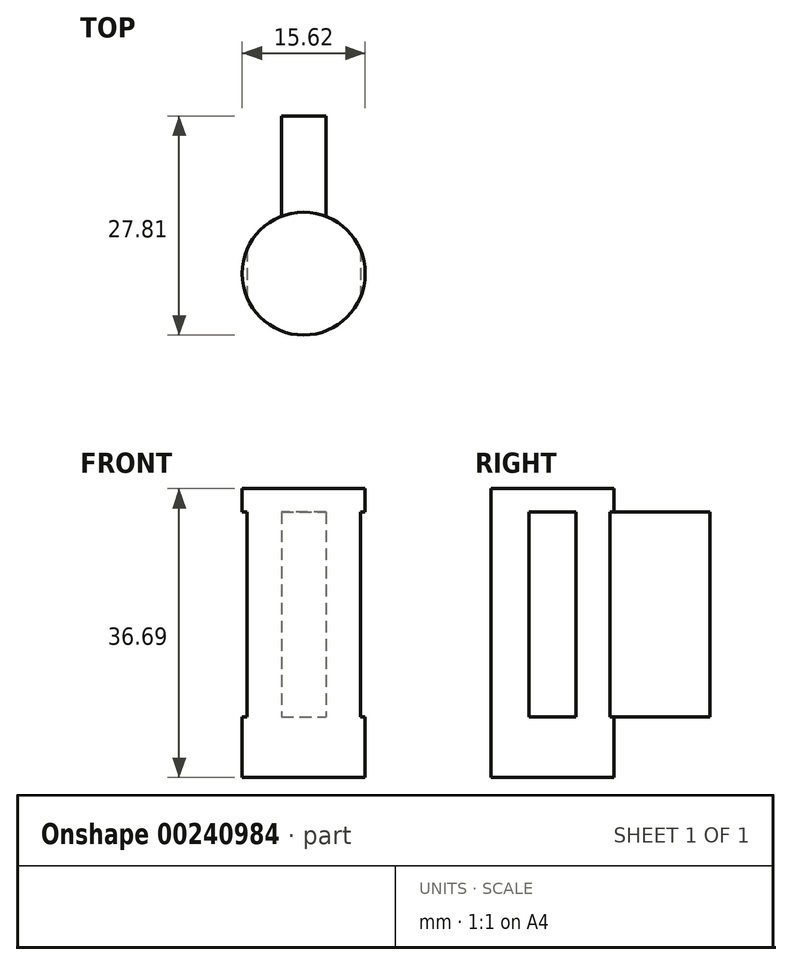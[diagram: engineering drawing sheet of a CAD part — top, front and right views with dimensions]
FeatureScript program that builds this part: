
annotation { "Feature Type Name" : "Feature", "Feature Type Description" : "" }
export const myFeature = defineFeature(function(context is Context, id is Id, definition is map)
    precondition{}
    {
        {
            var Q0;
            Q0=qCreatedBy(makeId("Top.planeOp"),FACE);
            var sketch = newSketch(context, id + "F0", { "sketchPlane" : qUnion([Q0])});
            skArc(sketch, "E0", {"start": v(-2.81, 7.29) * mm, "mid": v(-5.45, 5.6) * mm, "end": v(-7.21, 3) * mm});
            skLineSegment(sketch, "E1", {"start": v(0, 0) * mm, "end": v(0, 20) * mm, "construction": true});
            skLineSegment(sketch, "E2", {"start": v(-2.81, 20) * mm, "end": v(2.81, 20) * mm});
            skLineSegment(sketch, "E3", {"start": v(2.81, 20) * mm, "end": v(2.81, 7.29) * mm});
            skLineSegment(sketch, "E4", {"start": v(-2.81, 20) * mm, "end": v(-2.81, 7.29) * mm});
            skLineSegment(sketch, "E5", {"start": v(-7.81, 0) * mm, "end": v(7.81, 0) * mm});
            skLineSegment(sketch, "E6", {"start": v(7.21, 3) * mm, "end": v(7.21, -3) * mm});
            skLineSegment(sketch, "E7.MirrorCS", {"start": v(-7.21, 3) * mm, "end": v(-7.21, -3) * mm});
            skArc(sketch, "E8.trimOffspring", {"start": v(7.21, 3) * mm, "mid": v(5.45, 5.6) * mm, "end": v(2.81, 7.29) * mm});
            skArc(sketch, "E9.trimOffspring", {"start": v(-7.21, -3) * mm, "mid": v(0, -7.81) * mm, "end": v(7.21, -3) * mm});
            skSolve(sketch);
        }
        {
            var Q0;
            Q0 = qSketchRegion(id + "F0", true);
            extrude(context, id + "F1", {"entities" : qUnion([Q0]), "depth" : 26.04 * mm});
        }
        {
            var Q0;
            Q0=makeQuery(id+"F1.opExtrude","CAP_FACE",FACE,{"disambiguationData":[OSD([sQuery(id+"F0.wireOp",EDGE,"E0"),sQuery(id+"F0.wireOp",EDGE,"E2"),sQuery(id+"F0.wireOp",EDGE,"E3"),sQuery(id+"F0.wireOp",EDGE,"E4"),sQuery(id+"F0.wireOp",EDGE,"E6"),sQuery(id+"F0.wireOp",EDGE,"E7.MirrorCS"),sQuery(id+"F0.wireOp",EDGE,"E8.trimOffspring"),sQuery(id+"F0.wireOp",EDGE,"E9.trimOffspring")])],"isStart":false});
            var sketch = newSketch(context, id + "F2", { "sketchPlane" : qUnion([Q0])});
            skCircle(sketch, "E10", {"center": v(0, 0) * mm, "radius": 7.81 * mm});
            skSolve(sketch);
        }
        {
            var Q0;
            Q0 = qSketchRegion(id + "F2", true);
            extrude(context, id + "F3", {"entities" : qUnion([Q0]), "operationType" : NewBodyOperationType.ADD, "depth" : 3 * mm});
        }
        {
            var Q0;
            Q0=makeQuery(id+"F1.opExtrude","CAP_FACE",FACE,{"disambiguationData":[OSD([sQuery(id+"F0.wireOp",EDGE,"E0"),sQuery(id+"F0.wireOp",EDGE,"E2"),sQuery(id+"F0.wireOp",EDGE,"E3"),sQuery(id+"F0.wireOp",EDGE,"E4"),sQuery(id+"F0.wireOp",EDGE,"E6"),sQuery(id+"F0.wireOp",EDGE,"E7.MirrorCS"),sQuery(id+"F0.wireOp",EDGE,"E8.trimOffspring"),sQuery(id+"F0.wireOp",EDGE,"E9.trimOffspring")])],"isStart":true});
            var sketch = newSketch(context, id + "F4", { "sketchPlane" : qUnion([Q0])});
            skCircle(sketch, "E11", {"center": v(0, 0) * mm, "radius": 7.81 * mm});
            skSolve(sketch);
        }
        {
            var Q0;
            Q0 = qSketchRegion(id + "F4", true);
            extrude(context, id + "F5", {"entities" : qUnion([Q0]), "operationType" : NewBodyOperationType.ADD, "depth" : 7.65 * mm});
        }
    });
